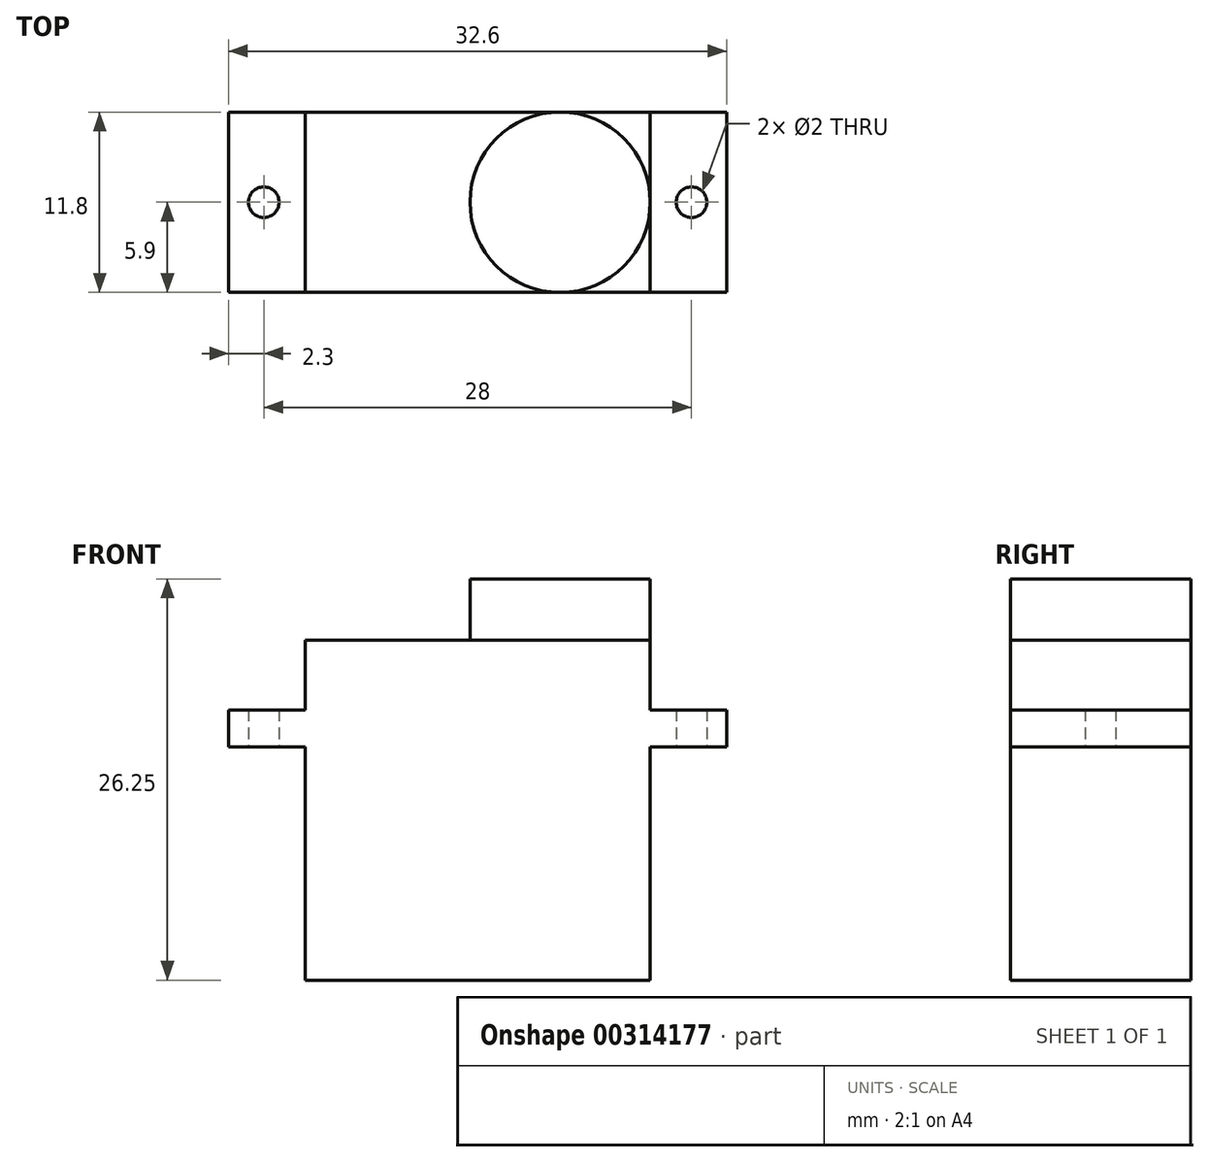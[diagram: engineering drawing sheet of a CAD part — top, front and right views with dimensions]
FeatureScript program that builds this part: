
annotation { "Feature Type Name" : "Feature", "Feature Type Description" : "" }
export const myFeature = defineFeature(function(context is Context, id is Id, definition is map)
    precondition{}
    {
        {
            var Q0;
            Q0=qCreatedBy(makeId("Top.planeOp"),FACE);
            var sketch = newSketch(context, id + "F0", { "sketchPlane" : qUnion([Q0])});
            skLineSegment(sketch, "E0.bottom", {"start": v(-16.7, 5.9) * mm, "end": v(5.9, 5.9) * mm});
            skLineSegment(sketch, "E0.top", {"start": v(-16.7, -5.9) * mm, "end": v(5.9, -5.9) * mm});
            skLineSegment(sketch, "E0.left", {"start": v(-16.7, 5.9) * mm, "end": v(-16.7, -5.9) * mm});
            skLineSegment(sketch, "E0.right", {"start": v(5.9, 5.9) * mm, "end": v(5.9, -5.9) * mm});
            skLineSegment(sketch, "E1.bottom", {"start": v(-16.7, 5.9) * mm, "end": v(-21.7, 5.9) * mm});
            skLineSegment(sketch, "E1.top", {"start": v(-16.7, -5.9) * mm, "end": v(-21.7, -5.9) * mm});
            skLineSegment(sketch, "E1.right", {"start": v(-21.7, 5.9) * mm, "end": v(-21.7, -5.9) * mm});
            skPoint(sketch, "E2.oppositeSnap0", {"position": v(-19.2, -5.9) * mm});
            skLineSegment(sketch, "E2.bottom", {"start": v(5.9, 5.9) * mm, "end": v(10.9, 5.9) * mm});
            skLineSegment(sketch, "E2.top", {"start": v(5.9, -5.9) * mm, "end": v(10.9, -5.9) * mm});
            skLineSegment(sketch, "E2.right", {"start": v(10.9, 5.9) * mm, "end": v(10.9, -5.9) * mm});
            skCircle(sketch, "E3", {"center": v(0, 0) * mm, "radius": 5.9 * mm});
            skCircle(sketch, "E4", {"center": v(-19.4, 0) * mm, "radius": 1 * mm});
            skPoint(sketch, "E4.centerSnap0", {"position": v(-16.7, 0) * mm});
            skCircle(sketch, "E5", {"center": v(8.6, 0) * mm, "radius": 1 * mm});
            skPoint(sketch, "E5.centerSnap0", {"position": v(10.9, 0) * mm});
            skPoint(sketch, "E6", {"position": v(-18.4, 0) * mm});
            skPoint(sketch, "E7", {"position": v(7.6, 0) * mm});
            skLineSegment(sketch, "E8", {"start": v(-21.7, 0) * mm, "end": v(-20.4, 0) * mm, "construction": true});
            skLineSegment(sketch, "E9", {"start": v(10.9, 0) * mm, "end": v(9.6, 0) * mm, "construction": true});
            skSolve(sketch);
        }
        {
            var Q0;
            Q0=makeQuery(id+"F0.imprint","IMPRINT",FACE,{"disambiguationData":[TD([[makeQuery(id+"F0.imprint","IMPRINT",EDGE,{"derivedFrom":sQuery(id+"F0.wireOp",EDGE,"E1.bottom")}),1.0]])]});
            var Q1;
            {var subQ0=sQuery(id+"F0.wireOp",EDGE,"E0.left");Q1=makeQuery(id+"F0.imprint","IMPRINT",FACE,{"disambiguationData":[TD([[makeQuery(id+"F0.imprint","IMPRINT",EDGE,{"derivedFrom":subQ0}),1.0]])]});}
            var Q2;
            {var subQ0=sQuery(id+"F0.wireOp",EDGE,"E3");var subQ1=makeQuery(id+"F0.imprint","INTERSECT",VERTEX,{"derivedFrom":[sQuery(id+"F0.wireOp",EDGE,"E0.bottom"),subQ0]});Q2=makeQuery(id+"F0.imprint","IMPRINT",FACE,{"disambiguationData":[TD([[makeQuery(id+"F0.imprint","IMPRINT",EDGE,{"disambiguationData":[TD([[subQ1,1.0]])],"derivedFrom":subQ0}),1.0]])]});}
            var Q3;
            {var subQ1=sQuery(id+"F0.wireOp",EDGE,"E0.bottom");var subQ3=sQuery(id+"F0.wireOp",EDGE,"E3");var subQ4=makeQuery(id+"F0.imprint","INTERSECT",VERTEX,{"derivedFrom":[subQ1,subQ3]});Q3=makeQuery(id+"F0.imprint","IMPRINT",FACE,{"disambiguationData":[TD([[makeQuery(id+"F0.imprint","IMPRINT",EDGE,{"disambiguationData":[TD([[subQ4,1.0]])],"derivedFrom":subQ3}),-1.0]])]});}
            var Q4;
            {var subQ1=sQuery(id+"F0.wireOp",EDGE,"E0.top");var subQ3=sQuery(id+"F0.wireOp",EDGE,"E3");var subQ4=makeQuery(id+"F0.imprint","INTERSECT",VERTEX,{"derivedFrom":[subQ1,subQ3]});Q4=makeQuery(id+"F0.imprint","IMPRINT",FACE,{"disambiguationData":[TD([[makeQuery(id+"F0.imprint","IMPRINT",EDGE,{"disambiguationData":[TD([[subQ4,-1.0]])],"derivedFrom":subQ3}),-1.0]])]});}
            var Q5;
            {var subQ3=sQuery(id+"F0.wireOp",EDGE,"E2.bottom");Q5=makeQuery(id+"F0.imprint","IMPRINT",FACE,{"disambiguationData":[TD([[makeQuery(id+"F0.imprint","IMPRINT",EDGE,{"derivedFrom":subQ3}),-1.0]])]});}
            extrude(context, id + "F1", {"entities" : qUnion([Q0, Q1, Q2, Q3, Q4, Q5]), "depth" : 2.43 * mm});
        }
        {
            var Q0;
            {var subQ0=sQuery(id+"F0.wireOp",EDGE,"E0.left");Q0=makeQuery(id+"F0.imprint","IMPRINT",FACE,{"disambiguationData":[TD([[makeQuery(id+"F0.imprint","IMPRINT",EDGE,{"derivedFrom":subQ0}),1.0]])]});}
            var Q1;
            {var subQ0=sQuery(id+"F0.wireOp",EDGE,"E3");var subQ1=makeQuery(id+"F0.imprint","INTERSECT",VERTEX,{"derivedFrom":[sQuery(id+"F0.wireOp",EDGE,"E0.bottom"),subQ0]});Q1=makeQuery(id+"F0.imprint","IMPRINT",FACE,{"disambiguationData":[TD([[makeQuery(id+"F0.imprint","IMPRINT",EDGE,{"disambiguationData":[TD([[subQ1,1.0]])],"derivedFrom":subQ0}),1.0]])]});}
            var Q2;
            {var subQ1=sQuery(id+"F0.wireOp",EDGE,"E0.top");var subQ3=sQuery(id+"F0.wireOp",EDGE,"E3");var subQ4=makeQuery(id+"F0.imprint","INTERSECT",VERTEX,{"derivedFrom":[subQ1,subQ3]});Q2=makeQuery(id+"F0.imprint","IMPRINT",FACE,{"disambiguationData":[TD([[makeQuery(id+"F0.imprint","IMPRINT",EDGE,{"disambiguationData":[TD([[subQ4,-1.0]])],"derivedFrom":subQ3}),-1.0]])]});}
            var Q3;
            {var subQ1=sQuery(id+"F0.wireOp",EDGE,"E0.bottom");var subQ3=sQuery(id+"F0.wireOp",EDGE,"E3");var subQ4=makeQuery(id+"F0.imprint","INTERSECT",VERTEX,{"derivedFrom":[subQ1,subQ3]});Q3=makeQuery(id+"F0.imprint","IMPRINT",FACE,{"disambiguationData":[TD([[makeQuery(id+"F0.imprint","IMPRINT",EDGE,{"disambiguationData":[TD([[subQ4,1.0]])],"derivedFrom":subQ3}),-1.0]])]});}
            extrude(context, id + "F2", {"entities" : qUnion([Q0, Q1, Q2, Q3]), "operationType" : NewBodyOperationType.ADD, "depth" : 7 * mm});
        }
        {
            var Q0;
            {var subQ0=sQuery(id+"F0.wireOp",EDGE,"E3");var subQ1=makeQuery(id+"F0.imprint","INTERSECT",VERTEX,{"derivedFrom":[sQuery(id+"F0.wireOp",EDGE,"E0.bottom"),subQ0]});Q0=makeQuery(id+"F0.imprint","IMPRINT",FACE,{"disambiguationData":[TD([[makeQuery(id+"F0.imprint","IMPRINT",EDGE,{"disambiguationData":[TD([[subQ1,1.0]])],"derivedFrom":subQ0}),1.0]])]});}
            extrude(context, id + "F3", {"entities" : qUnion([Q0]), "operationType" : NewBodyOperationType.ADD, "depth" : 11 * mm});
        }
        {
            var Q0;
            {var subQ0=sQuery(id+"F0.wireOp",EDGE,"E0.left");Q0=makeQuery(id+"F0.imprint","IMPRINT",FACE,{"disambiguationData":[TD([[makeQuery(id+"F0.imprint","IMPRINT",EDGE,{"derivedFrom":subQ0}),1.0]])]});}
            var Q1;
            {var subQ0=sQuery(id+"F0.wireOp",EDGE,"E3");var subQ1=makeQuery(id+"F0.imprint","INTERSECT",VERTEX,{"derivedFrom":[sQuery(id+"F0.wireOp",EDGE,"E0.bottom"),subQ0]});Q1=makeQuery(id+"F0.imprint","IMPRINT",FACE,{"disambiguationData":[TD([[makeQuery(id+"F0.imprint","IMPRINT",EDGE,{"disambiguationData":[TD([[subQ1,1.0]])],"derivedFrom":subQ0}),1.0]])]});}
            var Q2;
            {var subQ1=sQuery(id+"F0.wireOp",EDGE,"E0.top");var subQ3=sQuery(id+"F0.wireOp",EDGE,"E3");var subQ4=makeQuery(id+"F0.imprint","INTERSECT",VERTEX,{"derivedFrom":[subQ1,subQ3]});Q2=makeQuery(id+"F0.imprint","IMPRINT",FACE,{"disambiguationData":[TD([[makeQuery(id+"F0.imprint","IMPRINT",EDGE,{"disambiguationData":[TD([[subQ4,-1.0]])],"derivedFrom":subQ3}),-1.0]])]});}
            var Q3;
            {var subQ1=sQuery(id+"F0.wireOp",EDGE,"E0.bottom");var subQ3=sQuery(id+"F0.wireOp",EDGE,"E3");var subQ4=makeQuery(id+"F0.imprint","INTERSECT",VERTEX,{"derivedFrom":[subQ1,subQ3]});Q3=makeQuery(id+"F0.imprint","IMPRINT",FACE,{"disambiguationData":[TD([[makeQuery(id+"F0.imprint","IMPRINT",EDGE,{"disambiguationData":[TD([[subQ4,1.0]])],"derivedFrom":subQ3}),-1.0]])]});}
            extrude(context, id + "F4", {"entities" : qUnion([Q0, Q1, Q2, Q3]), "operationType" : NewBodyOperationType.ADD, "oppositeDirection" : true, "depth" : 15.25 * mm});
        }
    });
